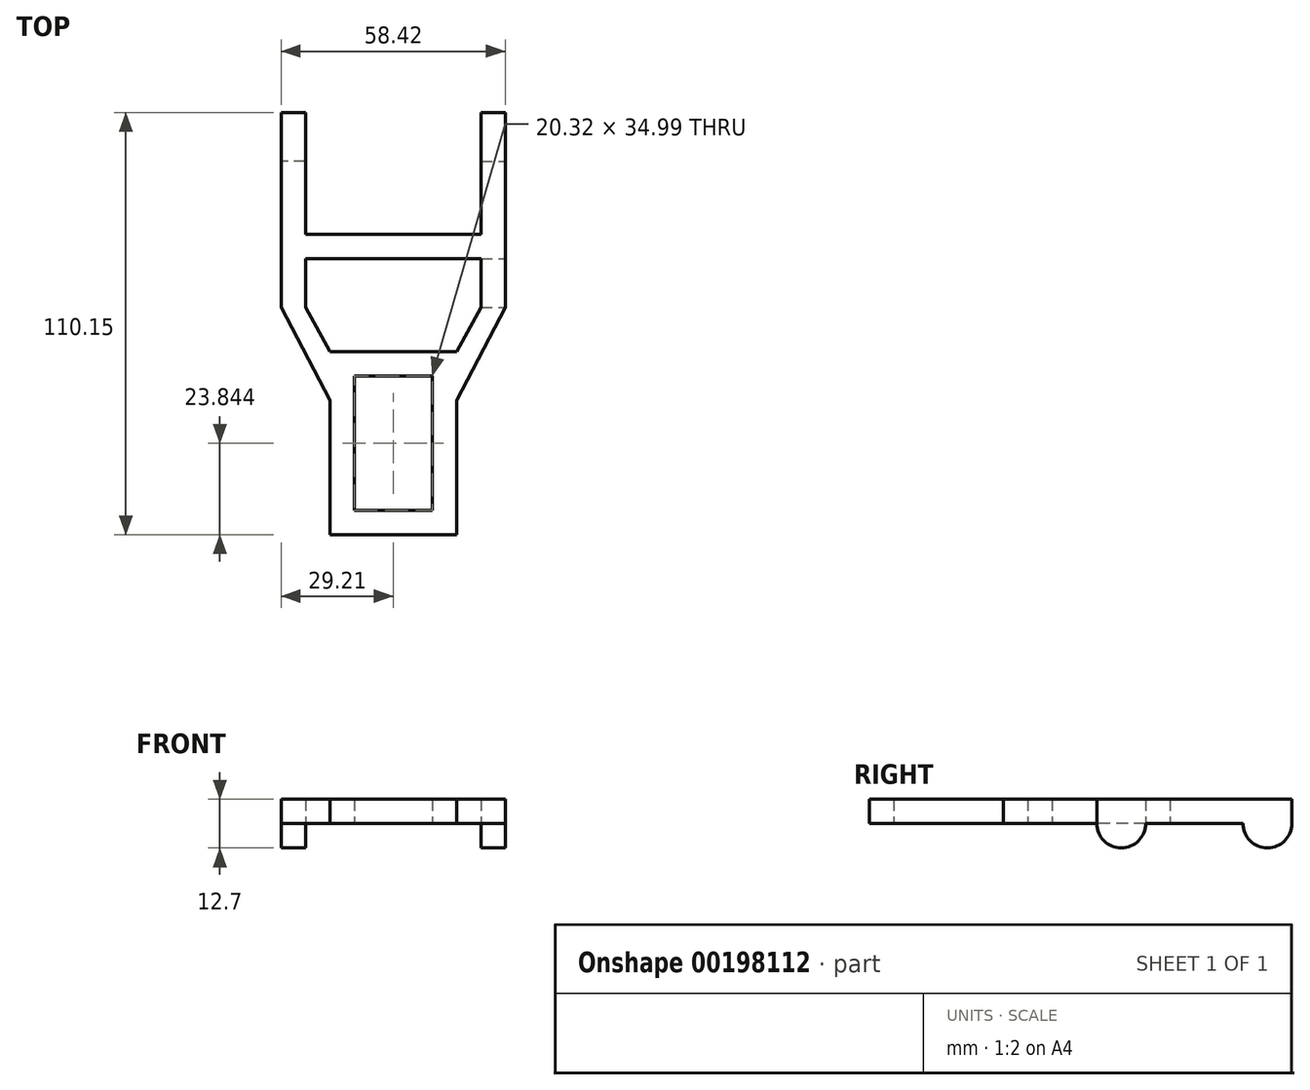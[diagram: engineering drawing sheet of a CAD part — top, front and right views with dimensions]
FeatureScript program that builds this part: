
annotation { "Feature Type Name" : "Feature", "Feature Type Description" : "" }
export const myFeature = defineFeature(function(context is Context, id is Id, definition is map)
    precondition{}
    {
        {
            var Q0;
            Q0=qCreatedBy(makeId("Top.planeOp"),FACE);
            var sketch = newSketch(context, id + "F0", { "sketchPlane" : qUnion([Q0])});
            skLineSegment(sketch, "E0.bottom", {"start": v(-29.21, 50.8) * mm, "end": v(-22.86, 50.8) * mm});
            skLineSegment(sketch, "E0.top", {"start": v(-29.21, 0) * mm, "end": v(-22.86, 0) * mm});
            skLineSegment(sketch, "E0.left", {"start": v(-29.21, 50.8) * mm, "end": v(-29.21, 0) * mm});
            skLineSegment(sketch, "E0.right", {"start": v(-22.86, 50.8) * mm, "end": v(-22.86, 0) * mm});
            skLineSegment(sketch, "E1.bottom", {"start": v(22.86, 50.8) * mm, "end": v(29.21, 50.8) * mm});
            skLineSegment(sketch, "E1.top", {"start": v(22.86, 0) * mm, "end": v(29.21, 0) * mm});
            skLineSegment(sketch, "E1.left", {"start": v(22.86, 50.8) * mm, "end": v(22.86, 0) * mm});
            skLineSegment(sketch, "E1.right", {"start": v(29.21, 50.8) * mm, "end": v(29.21, 0) * mm});
            skLineSegment(sketch, "E2", {"start": v(-29.21, 0) * mm, "end": v(-16.51, -24.36) * mm});
            skLineSegment(sketch, "E3.bottom", {"start": v(-16.51, -11.66) * mm, "end": v(16.51, -11.66) * mm});
            skLineSegment(sketch, "E3.top", {"start": v(-16.51, -59.35) * mm, "end": v(16.51, -59.35) * mm});
            skLineSegment(sketch, "E3.left", {"start": v(-16.51, -11.66) * mm, "end": v(-16.51, -59.35) * mm});
            skLineSegment(sketch, "E3.right", {"start": v(16.51, -11.66) * mm, "end": v(16.51, -59.35) * mm});
            skLineSegment(sketch, "E4.bottom", {"start": v(-10.16, -18.01) * mm, "end": v(10.16, -18.01) * mm});
            skLineSegment(sketch, "E4.top", {"start": v(-10.16, -53) * mm, "end": v(10.16, -53) * mm});
            skLineSegment(sketch, "E4.left", {"start": v(-10.16, -18.01) * mm, "end": v(-10.16, -53) * mm});
            skLineSegment(sketch, "E4.right", {"start": v(10.16, -18.01) * mm, "end": v(10.16, -53) * mm});
            skLineSegment(sketch, "E5", {"start": v(-22.86, 0) * mm, "end": v(-16.51, -11.66) * mm});
            skLineSegment(sketch, "E6", {"start": v(29.21, 0) * mm, "end": v(16.51, -24.36) * mm});
            skLineSegment(sketch, "E7", {"start": v(22.86, 0) * mm, "end": v(16.51, -11.66) * mm});
            skLineSegment(sketch, "E8", {"start": v(-22.86, 19.05) * mm, "end": v(22.86, 19.05) * mm});
            skLineSegment(sketch, "E9", {"start": v(-22.86, 12.7) * mm, "end": v(22.86, 12.7) * mm});
            skSolve(sketch);
        }
        {
            var Q0;
            Q0 = qSketchRegion(id + "F0", true);
            extrude(context, id + "F1", {"entities" : qUnion([Q0]), "depth" : 6.35 * mm});
        }
        {
            var Q0;
            Q0=makeQuery(id+"F1.opExtrude","SWEPT_FACE",FACE,{"disambiguationData":[OSD([sQuery(id+"F0.wireOp",EDGE,"E1.right")])]});
            var sketch = newSketch(context, id + "F2", { "sketchPlane" : qUnion([Q0])});
            skArc(sketch, "E10", {"start": v(38.1, 0) * mm, "mid": v(44.45, -6.35) * mm, "end": v(50.8, 0) * mm});
            skLineSegment(sketch, "E11", {"start": v(38.1, 0) * mm, "end": v(50.8, 0) * mm});
            skArc(sketch, "E12", {"start": v(0, 0) * mm, "mid": v(6.35, -6.35) * mm, "end": v(12.7, 0) * mm});
            skLineSegment(sketch, "E13", {"start": v(0, 0) * mm, "end": v(12.7, 0) * mm});
            skSolve(sketch);
        }
        {
            var Q0;
            Q0 = qSketchRegion(id + "F2", true);
            extrude(context, id + "F3", {"entities" : qUnion([Q0]), "operationType" : NewBodyOperationType.ADD, "oppositeDirection" : true, "depth" : 6.35 * mm});
        }
        {
            var Q0;
            Q0=makeQuery(id+"F1.opExtrude","SWEPT_FACE",FACE,{"disambiguationData":[OSD([sQuery(id+"F0.wireOp",EDGE,"E0.left")])]});
            var sketch = newSketch(context, id + "F4", { "sketchPlane" : qUnion([Q0])});
            skArc(sketch, "E14", {"start": v(-50.8, 0) * mm, "mid": v(-44.45, -6.35) * mm, "end": v(-38.1, 0) * mm});
            skLineSegment(sketch, "E15", {"start": v(-50.8, 0) * mm, "end": v(-38.1, 0) * mm});
            skSolve(sketch);
        }
        {
            var Q0;
            Q0 = qSketchRegion(id + "F4", true);
            extrude(context, id + "F5", {"entities" : qUnion([Q0]), "operationType" : NewBodyOperationType.ADD, "oppositeDirection" : true, "depth" : 6.35 * mm});
        }
    });
